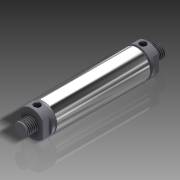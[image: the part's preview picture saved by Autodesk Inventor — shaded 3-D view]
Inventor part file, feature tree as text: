
AUTODESK INVENTOR PART (.ipt)
format: ipt  version: 2011 (Build 150239000, 239)  size: 164,864 bytes
history: native  units: in
note: dims shown in document units (in); Inventor stores cm internally (conversion verified against a paired STEP export)
features: thread x4, mirror x1, imported_body x1
ambient origin geometry x8: Origin, YZ Plane, XZ Plane, XY Plane, X Axis, Y Axis, Z Axis, Center Point
feature tree (6):
  mirror  "Mirror1"
  imported_body  "Base1"
  thread  "Thread1"  [1 undecoded]
  thread  "Thread2"  [1 undecoded]
  thread  "Thread3"  [1 undecoded]
  thread  "Thread4"  [1 undecoded]
note: 4 required parameter values undecoded (feature->parameter linkage not recoverable at this tier; creation-order binding heuristic only, values carry confidence <= 0.55)
